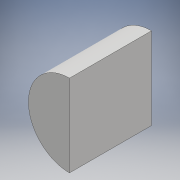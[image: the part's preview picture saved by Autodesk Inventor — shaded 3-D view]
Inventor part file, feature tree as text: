
AUTODESK INVENTOR PART (.ipt)
format: ipt  version: 2018 (Build 220112000, 112)  size: 88,064 bytes
history: native  units: mm
features: extrude x1, sketch x1
ambient origin geometry x8: Origin, YZ Plane, XZ Plane, XY Plane, X Axis, Y Axis, Z Axis, Center Point
bodies: Solid1 (feature_tree)
feature tree (2):
  extrude  "Extrusion1"  Depth=11.0mm TaperAngle=0.0deg
  sketch  "Sketch1"  dims[d0=11.0mm d1=11.0mm d2=0.0mm]
